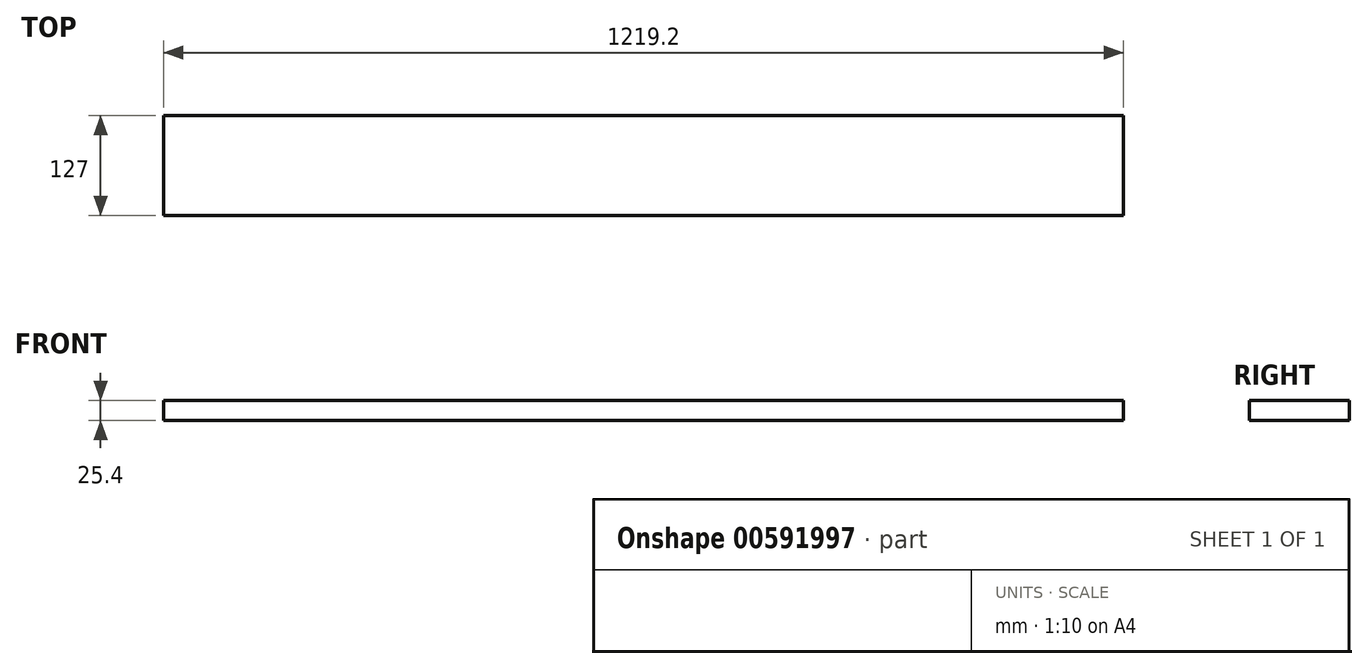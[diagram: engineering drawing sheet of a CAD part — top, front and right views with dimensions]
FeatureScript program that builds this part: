
annotation { "Feature Type Name" : "Feature", "Feature Type Description" : "" }
export const myFeature = defineFeature(function(context is Context, id is Id, definition is map)
    precondition{}
    {
        {
            var Q0;
            Q0=qCreatedBy(makeId("Top.planeOp"),FACE);
            var sketch = newSketch(context, id + "F0", { "sketchPlane" : qUnion([Q0])});
            skLineSegment(sketch, "E0.bottom", {"start": v(-523.99, -177.15) * mm, "end": v(695.21, -177.15) * mm});
            skLineSegment(sketch, "E0.top", {"start": v(-523.99, -304.15) * mm, "end": v(695.21, -304.15) * mm});
            skLineSegment(sketch, "E0.left", {"start": v(-523.99, -177.15) * mm, "end": v(-523.99, -304.15) * mm});
            skLineSegment(sketch, "E0.right", {"start": v(695.21, -177.15) * mm, "end": v(695.21, -304.15) * mm});
            skSolve(sketch);
        }
        {
            var Q0;
            Q0=makeQuery(id+"F0.imprint","IMPRINT",FACE,{"disambiguationData":[TD([[makeQuery(id+"F0.imprint","IMPRINT",EDGE,{"derivedFrom":sQuery(id+"F0.wireOp",EDGE,"E0.bottom")}),-1.0]])]});
            extrude(context, id + "F1", {"entities" : qUnion([Q0]), "depth" : 25.4 * mm, "offsetDistance" : 25.4 * mm});
        }
    });
